# Revit family: Haworth_Cappellini_Bac_Table_Round_AP_PRELIMINARY
name_source: partatom
category: Furniture
revit_build: Autodesk Revit 2018 (Build: 20170223_1515(x64)
units: mm (PartAtom-declared; Revit-internal decimal feet)

## family parameters
Always vertical = Yes
Cut with Voids When Loaded = No
OmniClass Number = 23.40.70.14.64.21
OmniClass Title = Systems Furniture
Room Calculation Point = No
Shared = No
Work Plane-Based = No

## types (1)
- Round Table
    Actual Depth = 1250 mm  [stored 4.10105 ft]
    Actual Height = 740 mm  [stored 2.42782 ft]
    Actual Width = 1250 mm  [stored 4.10105 ft]
    Assembly Code = E2020200
    Description = Haworth - Cappellini - Bac - Table - Round
    Leg Depth = 100 mm  [stored 0.328084 ft]
    Manufacturer = Haworth
    Model = BAC4
    Radius = 625 mm  [stored 2.05052 ft]
    Revision Number = 4
    Size = Verify Final Dim. w/ Haworth
    Support Depth = 60 mm
    Support Height = 110 mm  [stored 0.360892 ft]
    Table Thickness = 25 mm  [stored 0.082021 ft]
    URL = https://www.haworth.com
    URL - Product = https://www.haworth.com
    Warranty = http://www.haworth.com

note: [stored X ft] marks values corroborated as IEEE doubles in the binary element streams (Revit-internal decimal feet)

## geometry (parser evidence)
native form markers: Sweep x2
no freeform markers — native parametric forms only
